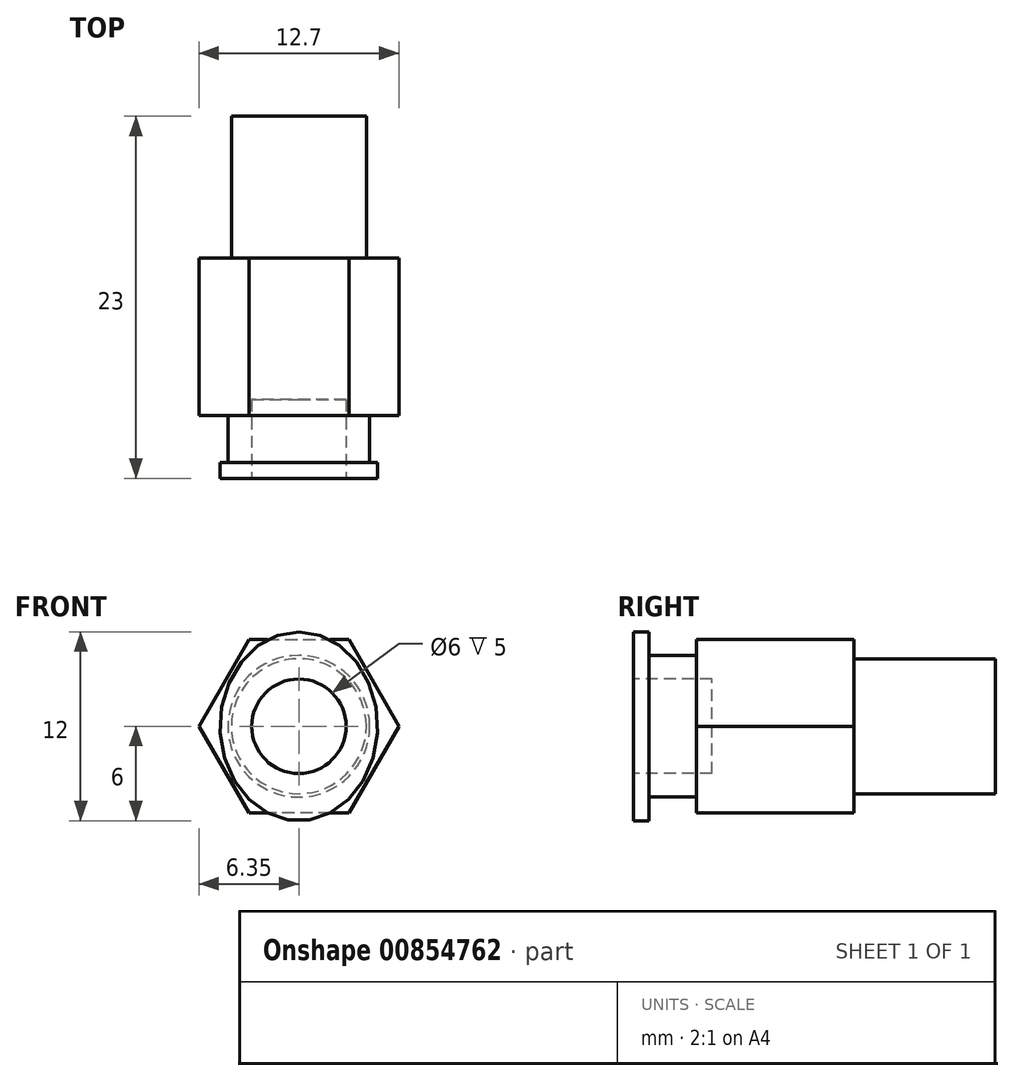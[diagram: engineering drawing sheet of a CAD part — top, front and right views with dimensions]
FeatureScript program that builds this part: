
annotation { "Feature Type Name" : "Feature", "Feature Type Description" : "" }
export const myFeature = defineFeature(function(context is Context, id is Id, definition is map)
    precondition{}
    {
        {
            var Q0;
            Q0=qCreatedBy(makeId("Front.planeOp"),FACE);
            var sketch = newSketch(context, id + "F0", { "sketchPlane" : qUnion([Q0])});
            skCircle(sketch, "E0", {"center": v(0, 0) * mm, "radius": 4.28 * mm});
            skSolve(sketch);
        }
        {
            var Q0;
            Q0=makeQuery(id+"F0.imprint","IMPRINT",FACE,{"disambiguationData":[TD([[makeQuery(id+"F0.imprint","IMPRINT",EDGE,{"derivedFrom":sQuery(id+"F0.wireOp",EDGE,"E0")}),1.0]])]});
            extrude(context, id + "F1", {"entities" : qUnion([Q0]), "depth" : 9 * mm, "offsetDistance" : 25 * mm});
        }
        {
            var Q0;
            Q0=makeQuery(id+"F1.opExtrude","CAP_FACE",FACE,{"disambiguationData":[OSD([sQuery(id+"F0.wireOp",EDGE,"E0")])],"isStart":false});
            var sketch = newSketch(context, id + "F2", { "sketchPlane" : qUnion([Q0])});
            skCircle(sketch, "E1.cCircle", {"center": v(0, 0) * mm, "radius": 5.5 * mm, "construction": true});
            skLineSegment(sketch, "E1.0", {"start": v(-3.18, 5.5) * mm, "end": v(3.18, 5.5) * mm});
            skLineSegment(sketch, "E1.1", {"start": v(3.18, 5.5) * mm, "end": v(6.35, 0) * mm});
            skLineSegment(sketch, "E1.2", {"start": v(6.35, 0) * mm, "end": v(3.18, -5.5) * mm});
            skLineSegment(sketch, "E1.3", {"start": v(3.18, -5.5) * mm, "end": v(-3.18, -5.5) * mm});
            skLineSegment(sketch, "E1.4", {"start": v(-3.18, -5.5) * mm, "end": v(-6.35, 0) * mm});
            skLineSegment(sketch, "E1.5", {"start": v(-6.35, 0) * mm, "end": v(-3.18, 5.5) * mm});
            skPoint(sketch, "E1.0.midPoint", {"position": v(0, 5.5) * mm});
            skSolve(sketch);
        }
        {
            var Q0;
            Q0=makeQuery(id+"F2.imprint","IMPRINT",FACE,{"disambiguationData":[TD([[makeQuery(id+"F2.imprint","IMPRINT",EDGE,{"derivedFrom":sQuery(id+"F2.wireOp",EDGE,"E1.0")}),-1.0]])]});
            var Q1;
            Q1=makeQuery(id+"F2.imprint","IMPRINT",FACE,{"disambiguationData":[TD([[makeQuery(id+"F2.imprint","IMPRINT",EDGE,{"derivedFrom":makeQuery(id+"F1.opExtrude","CAP_EDGE",EDGE,{"disambiguationData":[OSD([sQuery(id+"F0.wireOp",EDGE,"E0")])],"isStart":false})}),1.0]])]});
            extrude(context, id + "F3", {"entities" : qUnion([Q0, Q1]), "operationType" : NewBodyOperationType.ADD, "depth" : 10 * mm, "offsetDistance" : 25 * mm});
        }
        {
            var Q0;
            Q0=makeQuery(id+"F3.opExtrude","CAP_FACE",FACE,{"disambiguationData":[OSD([sQuery(id+"F2.wireOp",EDGE,"E1.0"),sQuery(id+"F2.wireOp",EDGE,"E1.1"),sQuery(id+"F2.wireOp",EDGE,"E1.2"),sQuery(id+"F2.wireOp",EDGE,"E1.3"),sQuery(id+"F2.wireOp",EDGE,"E1.4"),sQuery(id+"F2.wireOp",EDGE,"E1.5")])],"isStart":false});
            var sketch = newSketch(context, id + "F4", { "sketchPlane" : qUnion([Q0])});
            skCircle(sketch, "E2", {"center": v(0, 0) * mm, "radius": 4.5 * mm});
            skSolve(sketch);
        }
        {
            var Q0;
            Q0=makeQuery(id+"F4.imprint","IMPRINT",FACE,{"disambiguationData":[TD([[makeQuery(id+"F4.imprint","IMPRINT",EDGE,{"derivedFrom":sQuery(id+"F4.wireOp",EDGE,"E2")}),1.0]])]});
            var Q1;
            Q1 = qSketchRegion(id + "F6", true);
            extrude(context, id + "F5", {"entities" : qUnion([Q0, Q1]), "operationType" : NewBodyOperationType.ADD, "depth" : 3 * mm, "offsetDistance" : 25 * mm});
        }
        {
            var Q0;
            Q0=makeQuery(id+"F5.opExtrude","CAP_FACE",FACE,{"disambiguationData":[OSD([sQuery(id+"F4.wireOp",EDGE,"E2")])],"isStart":false});
            var sketch = newSketch(context, id + "F6", { "sketchPlane" : qUnion([Q0])});
            skEllipse(sketch, "E3", {"center": v(0, 0) * mm, "majorRadius": 6 * mm, "minorRadius": 5 * mm, "majorAxis": v(0, 1)});
            skSolve(sketch);
        }
        {
            var Q0;
            Q0 = qSketchRegion(id + "F6", true);
            extrude(context, id + "F7", {"entities" : qUnion([Q0]), "operationType" : NewBodyOperationType.ADD, "depth" : 1 * mm, "offsetDistance" : 25 * mm});
        }
        {
            var Q0;
            Q0=makeQuery(id+"F7.opExtrude","CAP_FACE",FACE,{"disambiguationData":[OSD([sQuery(id+"F6.wireOp",EDGE,"E3")])],"isStart":false});
            var sketch = newSketch(context, id + "F8", { "sketchPlane" : qUnion([Q0])});
            skCircle(sketch, "E4", {"center": v(0, 0) * mm, "radius": 3 * mm});
            skSolve(sketch);
        }
        {
            var Q0;
            Q0=makeQuery(id+"F8.imprint","IMPRINT",FACE,{"disambiguationData":[TD([[makeQuery(id+"F8.imprint","IMPRINT",EDGE,{"derivedFrom":sQuery(id+"F8.wireOp",EDGE,"E4")}),1.0]])]});
            extrude(context, id + "F9", {"entities" : qUnion([Q0]), "operationType" : NewBodyOperationType.REMOVE, "oppositeDirection" : true, "depth" : 5 * mm, "offsetDistance" : 25 * mm});
        }
    });
